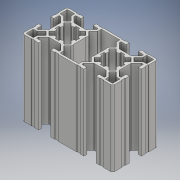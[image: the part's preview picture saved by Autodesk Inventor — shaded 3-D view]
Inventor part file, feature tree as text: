
AUTODESK INVENTOR PART (.ipt)
format: ipt  version: 2018 (Build 220112000, 112)  size: 576,000 bytes
history: native  units: mm
features: other x1, extrude x1, sketch x1
ambient origin geometry x8: Origin, YZ Plane, XZ Plane, XY Plane, X Axis, Y Axis, Z Axis, Center Point
bodies: Body1 (feature_tree)
feature tree (3):
  other  "Sólido1"
  extrude  "Extrusão1"  [1 undecoded]
  sketch  "Esboço1"  dims[d0=50.0mm d1=0.0mm]
note: 1 required parameter value undecoded (feature->parameter linkage not recoverable at this tier; creation-order binding heuristic only, values carry confidence <= 0.55)
